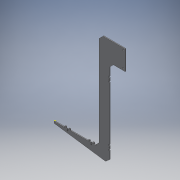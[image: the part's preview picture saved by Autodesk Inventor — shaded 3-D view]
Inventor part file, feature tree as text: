
AUTODESK INVENTOR PART (.ipt)
format: ipt  version: 2019 (Build 230136000, 136)  size: 332,800 bytes
history: native  units: in
note: dims shown in document units (in); Inventor stores cm internally (conversion verified against a paired STEP export)
features: reference x13, sketch x11, extrude x8, other x6, chamfer x2, projected_geometry x1, helix x1
ambient origin geometry x8: Origin, YZ Plane, XZ Plane, XY Plane, X Axis, Y Axis, Z Axis, Center Point
bodies: Solid1 (feature_tree)
feature tree (42):
  extrude  "Extrusion1"  Depth=0.1575in
  chamfer  "Chamfer1"  Distance=0.1575in
  chamfer  "Chamfer2"  Distance=0.7874in Angle=45.0deg
  sketch  "Sketch2"  dims[d7=0.7874in d8=0.125in d9=45.0deg d10=3.1496in]
  sketch  "Sketch3"  dims[d11=3.937in d12=1.0in d13=0.0in]
  sketch  "Sketch4"  dims[d14=0.126in d15=0.126in]
  extrude  "Extrusion2"  Depth=3.1496in
  extrude  "Extrusion3"  Depth=3.937in TaperAngle=0.0deg
  extrude  "Extrusion4"  Depth=0.126in
  sketch  "Sketch8"  dims[d26=0.0079in d27=0.0079in d28=0.2362in]
  extrude  "Extrusion5"  Depth=1.0in TaperAngle=0.0deg
  extrude  "Extrusion6"  Depth=1.0in TaperAngle=0.0deg
  extrude  "Extrusion7"  Depth=0.0079in
  extrude  "Extrusion8"  Depth=0.2362in
  sketch  "Sketch1"  dims[d0=15.748in d1=0.055in d2=0.1575in d3=0.0in d4=0.7874in d5=0.125in d6=45.0deg]
  reference  "Reference1"
  sketch  "Sketch5"  dims[d16=1.0in d17=0.0in d18=1.0in d19=0.0in]
  reference  "Reference2"
  reference  "Reference3"
  reference  "Reference4"
  reference  "Reference5"
  sketch  "Sketch6"  dims[d20=1.0in d21=0.0in d22=1.0in d23=0.0in]
  reference  "Reference6"
  reference  "Reference7"
  sketch  "Sketch7"  dims[d24=0.0079in d25=0.0079in]
  reference  "Reference8"
  reference  "Reference9"
  reference  "Reference10"
  sketch  "Sketch10"  dims[d29=0.2362in]
  reference  "Reference11"
  reference  "Reference12"
  sketch  "Sketch11"  dims[d30=0.3937in]
  reference  "Reference13"
  sketch  "Sketch12"  dims[d31=0.3937in d32=0.3937in d33=0.3937in d34=1.0in d35=0.0in d36=0.0079in d37=1.0in d38=0.0in]
  projected_geometry  "Projected Loop1"
  other  "<userpath>\Documents\CAD Files\Helix DLP\Helix DLP Z Stage.iam"
  helix  "Helix DLP Z Stage.iam"  [1 undecoded]
  other  "Print Platform:1"
  other  "Z stage_brace:1"
  other  "Maker_jigsaw_template:1"
  other  "Maker_jigsaw_template:2"
  other  "Z Stage_Linear Block Holder:1"
note: 1 required parameter value undecoded (feature->parameter linkage not recoverable at this tier; creation-order binding heuristic only, values carry confidence <= 0.55)
